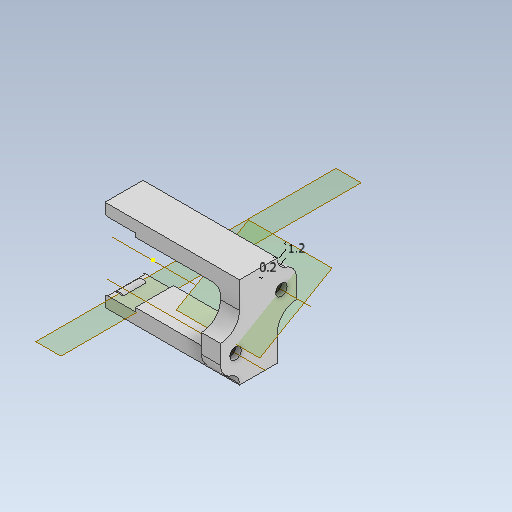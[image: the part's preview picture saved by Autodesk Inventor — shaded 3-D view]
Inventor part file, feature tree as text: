
AUTODESK INVENTOR PART (.ipt)
format: ipt  version: 2021 (Build 250183000, 183)  size: 239,104 bytes
history: native  units: in
note: dims shown in document units (in); Inventor stores cm internally (conversion verified against a paired STEP export)
features: reference x8, other x7, sketch x6, fillet x5, extrude x4, plane x2, projected_geometry x2, hole x1
ambient origin geometry x8: Origin, YZ Plane, XZ Plane, XY Plane, X Axis, Y Axis, Z Axis, Center Point
bodies: Body1 (feature_tree)
feature tree (35):
  other  "Work Axis2"
  extrude  "Extrusion3"  Depth=0.1181in
  extrude  "Extrusion4"  Depth=0.1969in
  hole  "Hole1"  [1 undecoded]
  extrude  "Extrusion5"  Depth=0.1181in
  plane  "Work Plane1"
  other  "Work Axis3"
  other  "Work Axis4"
  plane  "Work Plane2"
  sketch  "Sketch7"  dims[d20=0.3937in d21=0.0in]
  extrude  "Extrusion6"  Depth=0.1969in
  fillet  "Fillet1"  Radius=0.1378in
  fillet  "Fillet2"  Radius=0.0079in
  fillet  "Fillet3"  Radius=0.0472in
  fillet  "Fillet4"  Radius=0.0157in
  fillet  "Fillet5"  Radius=0.0787in
  sketch  "Sketch3"  dims[d11=0.1181in d12=0.1181in]
  reference  "Reference12"
  reference  "Reference13"
  reference  "Reference14"
  reference  "Reference15"
  reference  "Reference16"
  sketch  "Sketch4"  dims[d13=0.1575in d14=0.1969in]
  sketch  "Sketch5"  dims[d15=0.3937in d16=0.0in d17=0.7874in]
  reference  "Reference17"
  reference  "Reference18"
  sketch  "Sketch6"  dims[d18=0.1181in d19=0.1181in]
  projected_geometry  "Projected Loop1"
  projected_geometry  "Projected Loop2"
  sketch  "Sketch8"  dims[d22=0.1181in d23=0.2362in d24=0.1575in d25=0.0787in d26=90.0deg d27=0.315in d28=0.8108in d29=0.1969in d30=0.1378in d31=0.0in d32=0.0079in d33=0.0472in d34=0.0157in d35=0.0787in d36=0.0315in d37=0.2362in d38=0.0in d39=0.0276in d40=0.3543in d41=0.3543in d42=0.1969in d43=0.1575in d44=0.1181in d45=0.0787in d5=0.0197in d6=0.0344in d7=0.0197in d8=0.0344in]
  reference  "Reference19"
  other  "assy_gic_kinematic_2d_robot_arm_MK1_v2.iam"
  other  "sub_assy_robot_arm_link1:1"
  other  "arm_1_v2:1"
  other  "Pololu 1-2in Ball caster:1"
note: 1 required parameter value undecoded (feature->parameter linkage not recoverable at this tier; creation-order binding heuristic only, values carry confidence <= 0.55)
